# Revit family: Expansion_Joint-Glide_Plate-Inpro-300_Series-Floor_Wall
name_source: partatom
category: Generic Models
revit_build: Autodesk Revit 2018 (Build: 20170223_1515(x64)
units: mm (PartAtom-declared; Revit-internal decimal feet)

## family parameters
Can host rebar = No
Cut with Voids When Loaded = Yes
Host = Face
OmniClass Number = 23.20.30.24.21.14
OmniClass Title = Expansion Joints
Part Type = Normal
Room Calculation Point = No
Round Connector Dimension = Use Diameter
Shared = No

## types (5) — shared parameters
Bracket Material = Aluminum-Inpro
CSI MasterFormat Number = 07.95.13
CSI MasterFormat Title = Expansion Joint Cover Assemblies
Cover Material = Aluminum-Inpro
Default Elevation = 0' - 0"
Description = Floor/Wall - Movement: +/-50%
Fire Barrier = No
Inpro ISO# = BIMJM.032 REV2
Manufacturer = Inpro®
OmniClass Number = 23.20.30.24.21.14
OmniClass Title = Expansion Joint
URL = https://www.inprocorp.com
Vapor Barrier = No

## per-type parameters (varying)
| type | Blockout Width | Joint Width | Model | Plate Width | Sightline |
| 1" Joint | 0' - 2 3/4" | 0' - 1" | 300 - (300-A02-025) | 0' - 1 1/2" | 0' - 2 1/8" |
| 2" Joint | 0' - 3 1/4" | 0' - 2" | 300 - (300-A02-050) | 0' - 2 3/4" | 0' - 3 5/8" |
| 3" Joint | 0' - 3 3/4" | 0' - 3" | 300 - (300-A02-075) | 0' - 4" | 0' - 5 1/16" |
| 4" Joint | 0' - 4 1/4" | 0' - 4" | 300 - (300-A02-100) | 0' - 5 3/16" | 0' - 6 9/16" |
| 6" Joint | 0' - 5 1/4" | 0' - 6" | 300 - (300-A02-150) | 0' - 7 11/16" | 0' - 9 9/16" |

note: column(s) folded — value = type name in every type: Type Comments

## geometry (parser evidence)
native form markers: Sweep x2
no freeform markers — native parametric forms only
